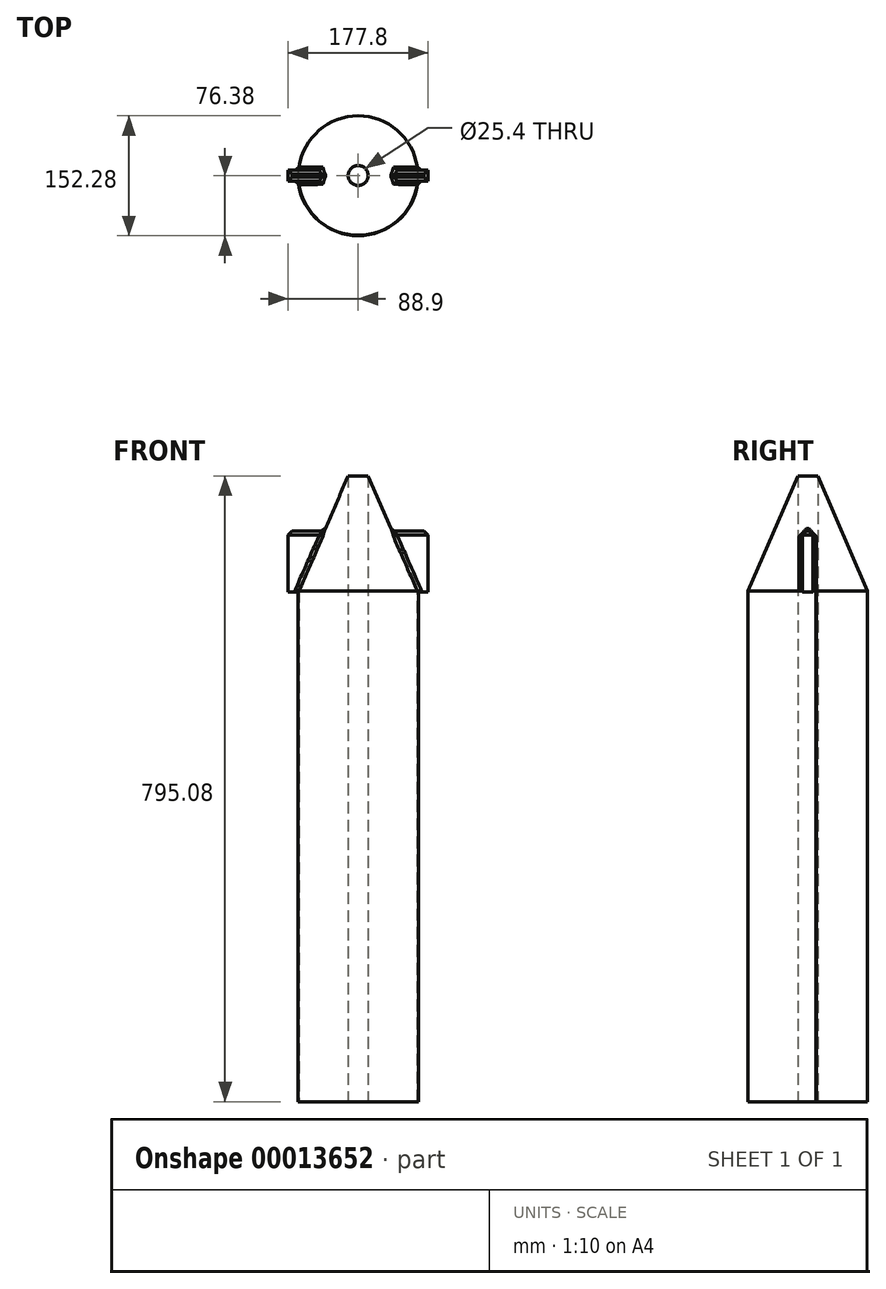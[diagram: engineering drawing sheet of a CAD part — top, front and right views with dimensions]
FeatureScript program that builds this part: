
annotation { "Feature Type Name" : "Feature", "Feature Type Description" : "" }
export const myFeature = defineFeature(function(context is Context, id is Id, definition is map)
    precondition{}
    {
        {
            var Q0;
            Q0=qCreatedBy(makeId("Front.planeOp"),FACE);
            var sketch = newSketch(context, id + "F0", { "sketchPlane" : qUnion([Q0])});
            skLineSegment(sketch, "E0", {"start": v(0, -76.1) * mm, "end": v(75.9, -76.1) * mm});
            skLineSegment(sketch, "E1", {"start": v(75.9, -76.1) * mm, "end": v(0, 99.3) * mm});
            skLineSegment(sketch, "E2", {"start": v(0, 99.3) * mm, "end": v(0, -76.1) * mm});
            skSolve(sketch);
        }
        {
            var Q0;
            Q0=makeQuery(id+"F0.imprint","IMPRINT",FACE,{"disambiguationData":[TD([[makeQuery(id+"F0.imprint","IMPRINT",EDGE,{"derivedFrom":sQuery(id+"F0.wireOp",EDGE,"E0")}),1.0]])]});
            var Q1;
            Q1=sQuery(id+"F0.wireOp",EDGE,"E2");
            revolve(context, id + "F1", {"entities" : qUnion([Q0]), "axis" : qUnion([Q1]), "revolveType" : RevolveType.FULL});
        }
        {
            var Q0;
            Q0=qCreatedBy(makeId("Right.planeOp"),FACE);
            var sketch = newSketch(context, id + "F2", { "sketchPlane" : qUnion([Q0])});
            skLineSegment(sketch, "E3.bottom", {"start": v(6.64, 0) * mm, "end": v(-7.07, 0) * mm});
            skLineSegment(sketch, "E3.top", {"start": v(6.64, -77.8) * mm, "end": v(-7.07, -77.8) * mm});
            skLineSegment(sketch, "E3.left", {"start": v(6.64, 0) * mm, "end": v(6.64, -77.8) * mm});
            skLineSegment(sketch, "E3.right", {"start": v(-7.07, 0) * mm, "end": v(-7.07, -77.8) * mm});
            skSolve(sketch);
        }
        {
            var Q0;
            Q0 = qSketchRegion(id + "F2", true);
            extrude(context, id + "F3", {"entities" : qUnion([Q0]), "operationType" : NewBodyOperationType.ADD, "endBound" : BoundingType.SYMMETRIC, "depth" : 177.8 * mm});
        }
        {
            var Q0;
            {var subQ0=sQuery(id+"F2.wireOp",EDGE,"E3.bottom");var subQ1=sQuery(id+"F2.wireOp",EDGE,"E3.right");var subQ2=sQuery(id+"F2.wireOp",EDGE,"E3.left");Q0=makeQuery(id+"F3.boolean.opBoolean","SPLIT",FACE,{"disambiguationData":[TD([makeQuery(id+"F3.opExtrude","CAP_FACE",FACE,{"disambiguationData":[OSD([subQ0,sQuery(id+"F2.wireOp",EDGE,"E3.top"),subQ2,subQ1])],"isStart":false})])],"derivedFrom":makeQuery(id+"F3.opExtrude","SWEPT_FACE",FACE,{"disambiguationData":[OSD([subQ0])]})});}
            var Q1;
            {var subQ0=sQuery(id+"F2.wireOp",EDGE,"E3.bottom");var subQ1=sQuery(id+"F2.wireOp",EDGE,"E3.right");var subQ2=sQuery(id+"F2.wireOp",EDGE,"E3.left");Q1=makeQuery(id+"F3.boolean.opBoolean","SPLIT",FACE,{"disambiguationData":[TD([makeQuery(id+"F3.opExtrude","CAP_FACE",FACE,{"disambiguationData":[OSD([subQ0,sQuery(id+"F2.wireOp",EDGE,"E3.top"),subQ2,subQ1])],"isStart":true})])],"derivedFrom":makeQuery(id+"F3.opExtrude","SWEPT_FACE",FACE,{"disambiguationData":[OSD([subQ0])]})});}
            chamfer(context, id + "F4", {"entities" : qUnion([Q0, Q1]), "width" : 5.08 * mm, "tangentPropagation" : true});
        }
        {
            var Q0;
            Q0=makeQuery(id+"F3.boolean.opBoolean","SPLIT",FACE,{"disambiguationData":[TD([makeQuery(id+"F3.opExtrude","SWEPT_FACE",FACE,{"disambiguationData":[OSD([sQuery(id+"F2.wireOp",EDGE,"E3.left")])]})])],"derivedFrom":makeQuery(id+"F1.opRevolve","SWEPT_FACE",FACE,{"disambiguationData":[OSD([sQuery(id+"F0.wireOp",EDGE,"E0")])]})});
            var sketch = newSketch(context, id + "F5", { "sketchPlane" : qUnion([Q0])});
            skCircle(sketch, "E4", {"center": v(0, 0) * mm, "radius": 76.38 * mm});
            skSolve(sketch);
        }
        {
            var Q0;
            {var subQ0=sQuery(id+"F0.wireOp",EDGE,"E0");var subQ2=makeQuery(id+"F3.opExtrude","SWEPT_FACE",FACE,{"disambiguationData":[OSD([sQuery(id+"F2.wireOp",EDGE,"E3.left")])]});var subQ7=sQuery(id+"F0.wireOp",EDGE,"E1");var subQ11=makeQuery(id+"F3.boolean.opBoolean","SPLIT",EDGE,{"disambiguationData":[TD([subQ2])],"derivedFrom":makeQuery(id+"F1.opRevolve","SWEPT_EDGE",EDGE,{"disambiguationData":[OSD([subQ0,subQ7])]})});Q0=makeQuery(id+"F5.imprint","IMPRINT",FACE,{"disambiguationData":[TD([[makeQuery(id+"F5.imprint","IMPRINT",EDGE,{"derivedFrom":subQ11}),-1.0]])]});}
            var Q1;
            {var subQ0=makeQuery(id+"F3.boolean.opBoolean","INTERSECT",EDGE,{"derivedFrom":[makeQuery(id+"F1.opRevolve","SWEPT_FACE",FACE,{"disambiguationData":[OSD([sQuery(id+"F0.wireOp",EDGE,"E0")])]}),makeQuery(id+"F3.opExtrude","SWEPT_FACE",FACE,{"disambiguationData":[OSD([sQuery(id+"F2.wireOp",EDGE,"E3.left")])]})]});var subQ1=sQuery(id+"F5.wireOp",EDGE,"E4");var subQ3=makeQuery(id+"F5.imprint","INTERSECT",VERTEX,{"disambiguationData":[OD(0.0)],"derivedFrom":[subQ0,subQ1]});Q1=makeQuery(id+"F5.imprint","IMPRINT",FACE,{"disambiguationData":[TD([[makeQuery(id+"F5.imprint","IMPRINT",EDGE,{"disambiguationData":[TD([[subQ3,1.0]])],"derivedFrom":subQ1}),1.0]])]});}
            extrude(context, id + "F6", {"entities" : qUnion([Q0, Q1]), "operationType" : NewBodyOperationType.ADD, "depth" : 649 * mm});
        }
        {
            var Q0;
            Q0=makeQuery(id+"F6.opExtrude","CAP_FACE",FACE,{"disambiguationData":[OSD([sQuery(id+"F0.wireOp",EDGE,"E0"),sQuery(id+"F0.wireOp",EDGE,"E1"),sQuery(id+"F2.wireOp",EDGE,"E3.left"),sQuery(id+"F5.wireOp",EDGE,"E4")])],"isStart":false});
            var sketch = newSketch(context, id + "F7", { "sketchPlane" : qUnion([Q0])});
            skCircle(sketch, "E5", {"center": v(0, 0) * mm, "radius": 12.7 * mm});
            skSolve(sketch);
        }
        {
            var Q0;
            Q0=makeQuery(id+"F7.imprint","IMPRINT",FACE,{"disambiguationData":[TD([[makeQuery(id+"F7.imprint","IMPRINT",EDGE,{"derivedFrom":sQuery(id+"F7.wireOp",EDGE,"E5")}),1.0]])]});
            extrude(context, id + "F8", {"entities" : qUnion([Q0]), "operationType" : NewBodyOperationType.REMOVE, "oppositeDirection" : true, "depth" : 866.03 * mm});
        }
    });
